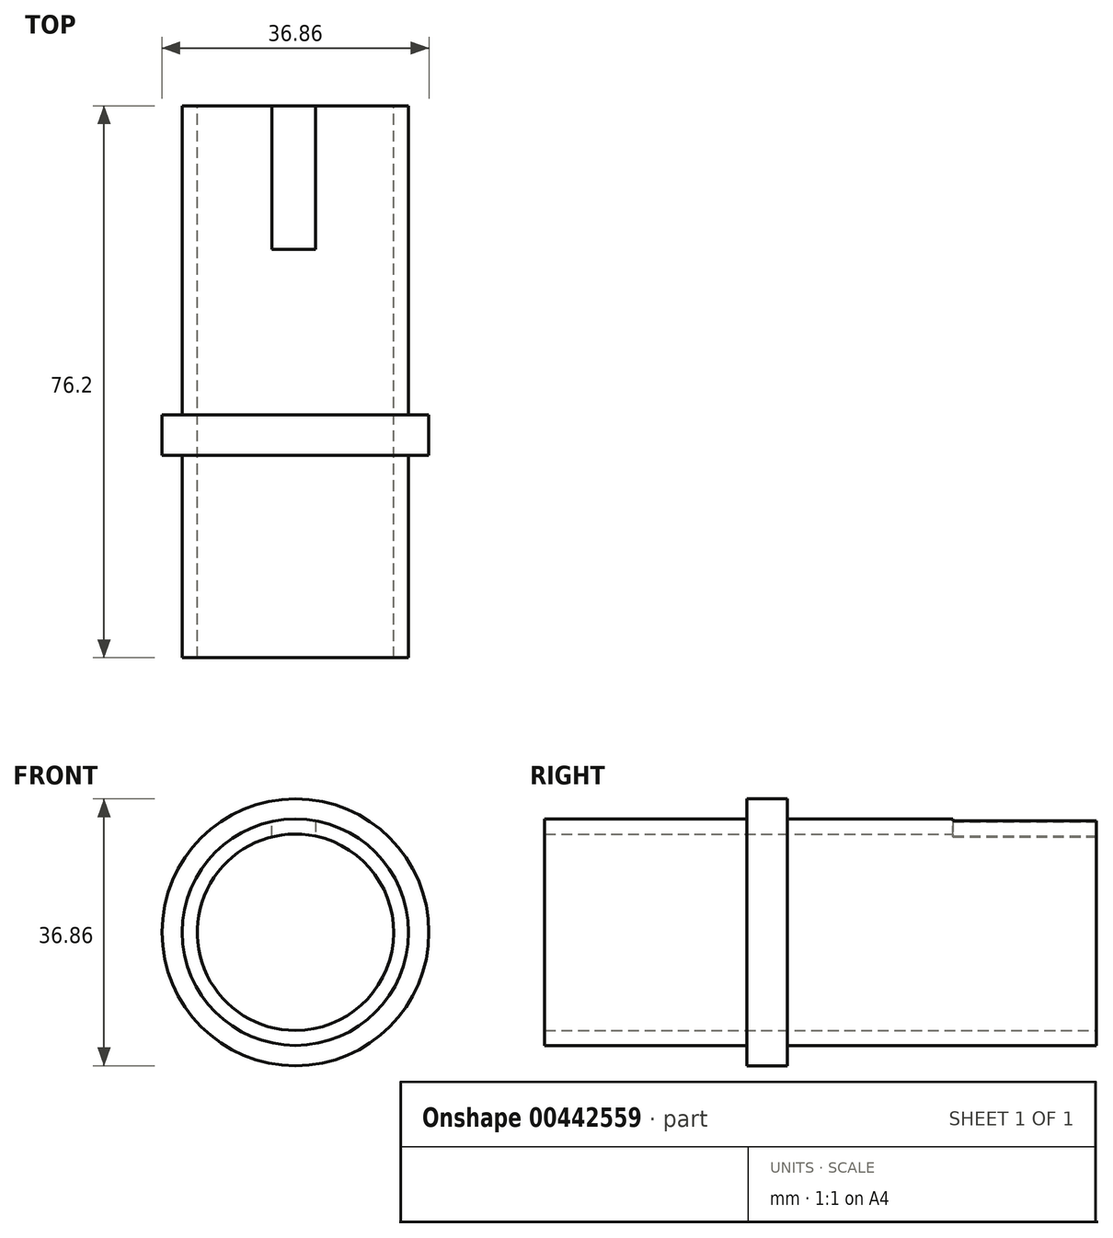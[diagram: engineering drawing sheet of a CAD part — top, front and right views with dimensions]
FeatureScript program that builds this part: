
annotation { "Feature Type Name" : "Feature", "Feature Type Description" : "" }
export const myFeature = defineFeature(function(context is Context, id is Id, definition is map)
    precondition{}
    {
        {
            var Q0;
            Q0=qCreatedBy(makeId("Front.planeOp"),FACE);
            var sketch = newSketch(context, id + "F0", { "sketchPlane" : qUnion([Q0])});
            skCircle(sketch, "E0", {"center": v(0, 0) * mm, "radius": 15.63 * mm});
            skCircle(sketch, "E1", {"center": v(0, 0) * mm, "radius": 13.56 * mm});
            skSolve(sketch);
        }
        {
            var Q0;
            Q0=makeQuery(id+"F0.imprint","IMPRINT",FACE,{"disambiguationData":[TD([[makeQuery(id+"F0.imprint","IMPRINT",EDGE,{"derivedFrom":sQuery(id+"F0.wireOp",EDGE,"E0")}),1.0]])]});
            extrude(context, id + "F1", {"entities" : qUnion([Q0]), "depth" : 76.2 * mm});
        }
        {
            var Q0;
            Q0=qCreatedBy(makeId("Front.planeOp"),FACE);
            var sketch = newSketch(context, id + "F2", { "sketchPlane" : qUnion([Q0])});
            skCircle(sketch, "E2", {"center": v(0, 0) * mm, "radius": 18.43 * mm});
            skCircle(sketch, "E3", {"center": v(0, 0) * mm, "radius": 15.63 * mm});
            skSolve(sketch);
        }
        {
            var Q0;
            Q0=makeQuery(id+"F2.imprint","IMPRINT",FACE,{"disambiguationData":[TD([[makeQuery(id+"F2.imprint","IMPRINT",EDGE,{"derivedFrom":sQuery(id+"F2.wireOp",EDGE,"E2")}),1.0]])]});
            extrude(context, id + "F3", {"entities" : qUnion([Q0]), "operationType" : NewBodyOperationType.ADD, "depth" : 48.26 * mm, "hasSecondDirection" : true, "secondDirectionOppositeDirection" : false, "secondDirectionDepth" : 42.67 * mm});
        }
        {
            var Q0;
            Q0=qCreatedBy(makeId("Front.planeOp"),FACE);
            var sketch = newSketch(context, id + "F4", { "sketchPlane" : qUnion([Q0])});
            skLineSegment(sketch, "E4", {"start": v(2.8, 15.82) * mm, "end": v(2.8, 13.02) * mm});
            skLineSegment(sketch, "E5", {"start": v(2.8, 13.02) * mm, "end": v(-3.26, 13.02) * mm});
            skLineSegment(sketch, "E6", {"start": v(-3.26, 13.02) * mm, "end": v(-3.26, 15.82) * mm});
            skLineSegment(sketch, "E7", {"start": v(-3.26, 15.82) * mm, "end": v(2.8, 15.82) * mm});
            skSolve(sketch);
        }
        {
            var Q0;
            Q0=makeQuery(id+"F4.imprint","IMPRINT",FACE,{"disambiguationData":[TD([[makeQuery(id+"F4.imprint","IMPRINT",EDGE,{"derivedFrom":sQuery(id+"F4.wireOp",EDGE,"E4")}),-1.0]])]});
            extrude(context, id + "F5", {"entities" : qUnion([Q0]), "operationType" : NewBodyOperationType.REMOVE, "depth" : 19.8 * mm});
        }
    });
